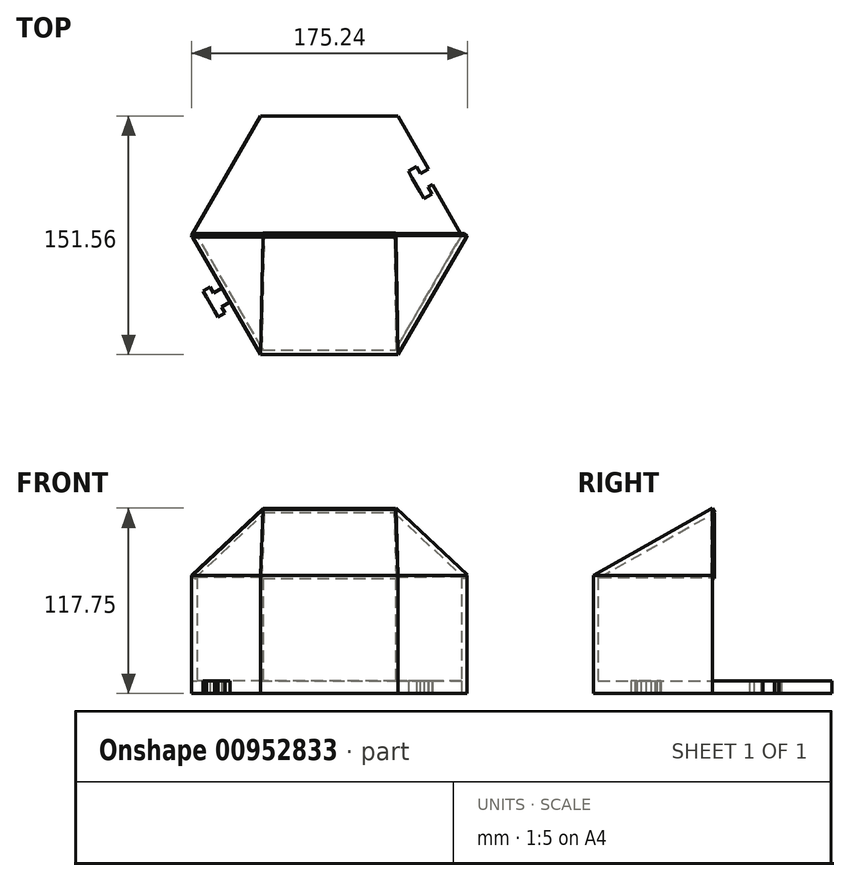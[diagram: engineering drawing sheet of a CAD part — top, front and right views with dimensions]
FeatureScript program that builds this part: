
annotation { "Feature Type Name" : "Feature", "Feature Type Description" : "" }
export const myFeature = defineFeature(function(context is Context, id is Id, definition is map)
    precondition{}
    {
        {
            var Q0;
            Q0=qCreatedBy(makeId("Top.planeOp"),FACE);
            var sketch = newSketch(context, id + "F0", { "sketchPlane" : qUnion([Q0])});
            skCircle(sketch, "E0.cCircle", {"center": v(0, 0) * mm, "radius": 75.78 * mm, "construction": true});
            skLineSegment(sketch, "E0.0", {"start": v(-43.75, 75.78) * mm, "end": v(43.75, 75.78) * mm});
            skLineSegment(sketch, "E0.1", {"start": v(43.75, 75.78) * mm, "end": v(87.5, 0) * mm});
            skLineSegment(sketch, "E0.2", {"start": v(87.5, 0) * mm, "end": v(43.75, -75.78) * mm});
            skLineSegment(sketch, "E0.3", {"start": v(43.75, -75.78) * mm, "end": v(-43.75, -75.78) * mm});
            skLineSegment(sketch, "E0.4", {"start": v(-43.75, -75.78) * mm, "end": v(-87.5, 0) * mm});
            skLineSegment(sketch, "E0.5", {"start": v(-87.5, 0) * mm, "end": v(-43.75, 75.78) * mm});
            skPoint(sketch, "E0.0.midPoint", {"position": v(0, 75.78) * mm});
            skLineSegment(sketch, "E1.0", {"start": v(-84.04, 0) * mm, "end": v(-42.02, 72.78) * mm});
            skLineSegment(sketch, "E1.1", {"start": v(42.02, 72.78) * mm, "end": v(84.04, 0) * mm});
            skLineSegment(sketch, "E1.2", {"start": v(84.04, 0) * mm, "end": v(42.02, -72.78) * mm});
            skLineSegment(sketch, "E1.3", {"start": v(-42.02, 72.78) * mm, "end": v(42.02, 72.78) * mm});
            skLineSegment(sketch, "E1.4", {"start": v(42.02, -72.78) * mm, "end": v(-42.02, -72.78) * mm});
            skLineSegment(sketch, "E1.5", {"start": v(-42.02, -72.78) * mm, "end": v(-84.04, 0) * mm});
            skLineSegment(sketch, "E2", {"start": v(-87.5, 0) * mm, "end": v(-84.04, 0) * mm});
            skLineSegment(sketch, "E3", {"start": v(84.04, 0) * mm, "end": v(87.5, 0) * mm});
            skLineSegment(sketch, "E4", {"start": v(0, 0) * mm, "end": v(0, 72.78) * mm, "construction": true});
            skLineSegment(sketch, "E5", {"start": v(0, 0) * mm, "end": v(42.02, 72.78) * mm, "construction": true});
            skLineSegment(sketch, "E6", {"start": v(0, 0) * mm, "end": v(-42.02, 72.78) * mm, "construction": true});
            skLineSegment(sketch, "E7", {"start": v(0, 36.39) * mm, "end": v(0, 72.78) * mm, "construction": true});
            skLineSegment(sketch, "E8.bottom", {"start": v(25, 48.33) * mm, "end": v(-25, 48.33) * mm});
            skLineSegment(sketch, "E8.top", {"start": v(25, 60.83) * mm, "end": v(-25, 60.83) * mm});
            skLineSegment(sketch, "E8.left", {"start": v(25, 48.33) * mm, "end": v(25, 60.83) * mm});
            skLineSegment(sketch, "E8.right", {"start": v(-25, 48.33) * mm, "end": v(-25, 60.83) * mm});
            skPoint(sketch, "E8.middle", {"position": v(0, 54.58) * mm});
            skLineSegment(sketch, "E9", {"start": v(-65.63, 37.89) * mm, "end": v(-68.13, 33.56) * mm});
            skLineSegment(sketch, "E10.MirrorCS", {"start": v(55.16, 32) * mm, "end": v(57.62, 27.65) * mm});
            skLineSegment(sketch, "E11.MirrorCS", {"start": v(55.16, 32) * mm, "end": v(52.71, 36.37) * mm});
            skLineSegment(sketch, "E12.MirrorCS", {"start": v(57.62, 27.65) * mm, "end": v(68.13, 33.56) * mm});
            skLineSegment(sketch, "E13.MirrorCS", {"start": v(87.5, 0) * mm, "end": v(43.75, 75.78) * mm});
            skLineSegment(sketch, "E14.MirrorCS", {"start": v(52.71, 36.37) * mm, "end": v(63.12, 42.22) * mm});
            skLineSegment(sketch, "E15.MirrorCS", {"start": v(57.97, 39.32) * mm, "end": v(55.52, 43.68) * mm});
            skLineSegment(sketch, "E16.MirrorCS", {"start": v(55.52, 43.68) * mm, "end": v(50.26, 40.72) * mm});
            skLineSegment(sketch, "E17.MirrorCS", {"start": v(52.71, 36.37) * mm, "end": v(50.26, 40.72) * mm});
            skLineSegment(sketch, "E18.MirrorCS", {"start": v(57.62, 27.65) * mm, "end": v(60.07, 23.3) * mm});
            skLineSegment(sketch, "E19.MirrorCS", {"start": v(62.87, 30.6) * mm, "end": v(65.32, 26.25) * mm});
            skLineSegment(sketch, "E20.MirrorCS", {"start": v(65.32, 26.25) * mm, "end": v(60.07, 23.3) * mm});
            skLineSegment(sketch, "E21.MirrorCS", {"start": v(-77.85, -39.32) * mm, "end": v(-68.12, -33.56) * mm});
            skLineSegment(sketch, "E22.MirrorCS", {"start": v(-73.54, -36.77) * mm, "end": v(-75.84, -32.9) * mm});
            skLineSegment(sketch, "E23.MirrorCS", {"start": v(-75.84, -32.9) * mm, "end": v(-80.14, -35.45) * mm});
            skLineSegment(sketch, "E24.MirrorCS", {"start": v(-77.85, -39.32) * mm, "end": v(-80.14, -35.45) * mm});
            skLineSegment(sketch, "E25.MirrorCS", {"start": v(-77.85, -39.32) * mm, "end": v(-72.85, -47.98) * mm});
            skLineSegment(sketch, "E26.MirrorCS", {"start": v(-72.85, -47.98) * mm, "end": v(-70.55, -51.85) * mm});
            skLineSegment(sketch, "E27.MirrorCS", {"start": v(-66.25, -49.3) * mm, "end": v(-70.55, -51.85) * mm});
            skLineSegment(sketch, "E28.MirrorCS", {"start": v(-72.85, -47.98) * mm, "end": v(-63.13, -42.22) * mm});
            skPoint(sketch, "E29.endSnap0", {"position": v(-67.99, -45.1) * mm});
            skLineSegment(sketch, "E30", {"start": v(-72.85, -47.98) * mm, "end": v(-68.54, -45.43) * mm});
            skLineSegment(sketch, "E31", {"start": v(-66.25, -49.3) * mm, "end": v(-68.54, -45.43) * mm});
            skSolve(sketch);
        }
        {
            var Q0;
            Q0=makeQuery(id+"F0.imprint","IMPRINT",FACE,{"disambiguationData":[TD([[makeQuery(id+"F0.imprint","IMPRINT",EDGE,{"derivedFrom":sQuery(id+"F0.wireOp",EDGE,"E1.0")}),-1.0]])]});
            extrude(context, id + "F1", {"entities" : qUnion([Q0]), "depth" : 8 * mm, "offsetDistance" : 25 * mm});
        }
        {
            var Q0;
            Q0=makeQuery(id+"F0.imprint","IMPRINT",FACE,{"disambiguationData":[TD([[makeQuery(id+"F0.imprint","IMPRINT",EDGE,{"derivedFrom":sQuery(id+"F0.wireOp",EDGE,"E0.2")}),-1.0]])]});
            extrude(context, id + "F2", {"entities" : qUnion([Q0]), "operationType" : NewBodyOperationType.ADD, "depth" : 75 * mm, "offsetDistance" : 25 * mm});
        }
        {
            var Q0;
            Q0=qCreatedBy(makeId("Front.planeOp"),FACE);
            var sketch = newSketch(context, id + "F3", { "sketchPlane" : qUnion([Q0])});
            skLineSegment(sketch, "E32", {"start": v(0, 0) * mm, "end": v(0, 144.27) * mm, "construction": true});
            skLineSegment(sketch, "E33", {"start": v(0, 144.27) * mm, "end": v(-94, 144.27) * mm, "construction": true});
            skLineSegment(sketch, "E34", {"start": v(0, 144.27) * mm, "end": v(81.74, 144.27) * mm});
            skLineSegment(sketch, "E35", {"start": v(0, 0) * mm, "end": v(0, 75) * mm, "construction": true});
            skLineSegment(sketch, "E36", {"start": v(0, 75) * mm, "end": v(0, 114.5) * mm, "construction": true});
            skLineSegment(sketch, "E37", {"start": v(0, 75) * mm, "end": v(-87.5, 75) * mm, "construction": true});
            skLineSegment(sketch, "E38", {"start": v(0, 114.5) * mm, "end": v(42.02, 114.5) * mm, "construction": true});
            skLineSegment(sketch, "E39", {"start": v(0, 114.5) * mm, "end": v(-42.02, 114.5) * mm});
            skLineSegment(sketch, "E40", {"start": v(0, 75) * mm, "end": v(-84.04, 75) * mm, "construction": true});
            skLineSegment(sketch, "E41", {"start": v(-42.02, 114.5) * mm, "end": v(-84.04, 75) * mm});
            skLineSegment(sketch, "E42", {"start": v(-42.02, 114.5) * mm, "end": v(-42.02, 117.5) * mm, "construction": true});
            skLineSegment(sketch, "E43", {"start": v(-42.02, 117.5) * mm, "end": v(-87.5, 75) * mm});
            skLineSegment(sketch, "E44", {"start": v(-42.02, 117.5) * mm, "end": v(0, 117.5) * mm});
            skLineSegment(sketch, "E45.MirrorCS", {"start": v(42.02, 117.5) * mm, "end": v(87.5, 75) * mm});
            skLineSegment(sketch, "E46.MirrorCS", {"start": v(42.02, 114.5) * mm, "end": v(84.04, 75) * mm});
            skLineSegment(sketch, "E47.MirrorCS", {"start": v(42.02, 117.5) * mm, "end": v(0, 117.5) * mm});
            skLineSegment(sketch, "E48.MirrorCS", {"start": v(0, 114.5) * mm, "end": v(42.02, 114.5) * mm});
            skLineSegment(sketch, "E49", {"start": v(87.5, 75) * mm, "end": v(84.04, 75) * mm});
            skLineSegment(sketch, "E50", {"start": v(-84.04, 75) * mm, "end": v(-87.5, 75) * mm});
            skSolve(sketch);
        }
        {
            var Q0;
            Q0=makeQuery(id+"F0.imprint","IMPRINT",FACE,{"disambiguationData":[TD([[makeQuery(id+"F0.imprint","IMPRINT",EDGE,{"derivedFrom":sQuery(id+"F0.wireOp",EDGE,"E0.0")}),-1.0]])]});
            extrude(context, id + "F4", {"entities" : qUnion([Q0]), "operationType" : NewBodyOperationType.ADD, "oppositeDirection" : true, "depth" : -8 * mm, "offsetDistance" : 25 * mm});
        }
        {
            var Q0;
            Q0=makeQuery(id+"F2.opExtrude","CAP_EDGE",EDGE,{"disambiguationData":[OSD([sQuery(id+"F0.wireOp",EDGE,"E0.3")])],"isStart":false});
            var Q1;
            Q1=sQuery(id+"F3.wireOp",VERTEX,"E44.end");
            cPlane(context, id + "F5", {"entities" : qUnion([Q0, Q1]), "cplaneType" : CPlaneType.LINE_ANGLE, "offset" : 25 * mm, "angle" : 0 * degree, "width" : 150 * mm, "height" : 150 * mm});
        }
        {
            var Q0;
            Q0=qCreatedBy(id+"F5.planeOp",FACE);
            var sketch = newSketch(context, id + "F6", { "sketchPlane" : qUnion([Q0])});
            skLineSegment(sketch, "E51", {"start": v(0, 29.4) * mm, "end": v(43.75, 29.4) * mm});
            skLineSegment(sketch, "E52", {"start": v(0, 29.4) * mm, "end": v(-43.75, 29.4) * mm});
            skLineSegment(sketch, "E53", {"start": v(-43.75, 29.4) * mm, "end": v(-42.02, -57.48) * mm});
            skLineSegment(sketch, "E54", {"start": v(43.75, 29.4) * mm, "end": v(42.02, -57.48) * mm});
            skLineSegment(sketch, "E55", {"start": v(-42.02, -57.48) * mm, "end": v(42.02, -57.48) * mm});
            skSolve(sketch);
        }
        {
            var Q0;
            Q0=makeQuery(id+"F6.imprint","IMPRINT",FACE,{"disambiguationData":[TD([[makeQuery(id+"F6.imprint","IMPRINT",EDGE,{"derivedFrom":sQuery(id+"F6.wireOp",EDGE,"E51")}),-1.0]])]});
            extrude(context, id + "F7", {"entities" : qUnion([Q0]), "operationType" : NewBodyOperationType.ADD, "depth" : 3 * mm, "offsetDistance" : 25 * mm});
        }
        {
            var Q0;
            Q0=makeQuery(id+"F3.imprint","IMPRINT",FACE,{"disambiguationData":[TD([[makeQuery(id+"F3.imprint","IMPRINT",EDGE,{"derivedFrom":sQuery(id+"F3.wireOp",EDGE,"E39")}),-1.0]])]});
            extrude(context, id + "F8", {"entities" : qUnion([Q0]), "operationType" : NewBodyOperationType.ADD, "depth" : 1 * mm, "offsetDistance" : 25 * mm});
        }
        {
            var Q0;
            Q0=makeQuery(id+"F8.opExtrude","CAP_EDGE",EDGE,{"disambiguationData":[OSD([sQuery(id+"F3.wireOp",EDGE,"E43")])],"isStart":true});
            var Q1;
            Q1=makeQuery(id+"F7.boolean.opBoolean","MERGE",VERTEX,{"derivedFrom":[makeQuery(id+"F2.opExtrude","CAP_VERTEX",VERTEX,{"disambiguationData":[OSD([sQuery(id+"F0.wireOp",EDGE,"E0.3"),sQuery(id+"F0.wireOp",EDGE,"E0.4")])],"isStart":false}),makeQuery(id+"F7.opExtrude","CAP_VERTEX",VERTEX,{"disambiguationData":[OSD([sQuery(id+"F6.wireOp",EDGE,"E52"),sQuery(id+"F6.wireOp",EDGE,"E53")])],"isStart":true})]});
            cPlane(context, id + "F9", {"entities" : qUnion([Q0, Q1]), "cplaneType" : CPlaneType.LINE_ANGLE, "offset" : 25 * mm, "angle" : 0 * degree, "width" : 150 * mm, "height" : 150 * mm});
        }
        {
            var Q0;
            Q0=qCreatedBy(id+"F9.planeOp",FACE);
            var sketch = newSketch(context, id + "F10", { "sketchPlane" : qUnion([Q0])});
            skLineSegment(sketch, "E56", {"start": v(-25.66, 35.61) * mm, "end": v(30.99, -31.08) * mm});
            skLineSegment(sketch, "E57", {"start": v(-25.66, 35.61) * mm, "end": v(33.23, 55.79) * mm});
            skLineSegment(sketch, "E58", {"start": v(33.23, 55.79) * mm, "end": v(30.99, -31.08) * mm});
            skSolve(sketch);
        }
        {
            var Q0;
            Q0=qSketchRegion(id+"F10",true);
            extrude(context, id + "F11", {"entities" : qUnion([Q0]), "operationType" : NewBodyOperationType.ADD, "depth" : -3 * mm, "offsetDistance" : 25 * mm});
        }
        {
            var Q0;
            Q0=makeQuery(id+"F8.opExtrude","CAP_EDGE",EDGE,{"disambiguationData":[OSD([sQuery(id+"F3.wireOp",EDGE,"E45.MirrorCS")])],"isStart":false});
            var Q1;
            Q1=makeQuery(id+"F7.boolean.opBoolean","MERGE",VERTEX,{"derivedFrom":[makeQuery(id+"F2.opExtrude","CAP_VERTEX",VERTEX,{"disambiguationData":[OSD([sQuery(id+"F0.wireOp",EDGE,"E0.2"),sQuery(id+"F0.wireOp",EDGE,"E0.3")])],"isStart":false}),makeQuery(id+"F7.opExtrude","CAP_VERTEX",VERTEX,{"disambiguationData":[OSD([sQuery(id+"F6.wireOp",EDGE,"E51"),sQuery(id+"F6.wireOp",EDGE,"E54")])],"isStart":true})]});
            cPlane(context, id + "F12", {"entities" : qUnion([Q0, Q1]), "cplaneType" : CPlaneType.LINE_ANGLE, "offset" : 25 * mm, "angle" : 0 * degree, "width" : 150 * mm, "height" : 150 * mm});
        }
        {
            var Q0;
            Q0=qCreatedBy(id+"F12.planeOp",FACE);
            var sketch = newSketch(context, id + "F13", { "sketchPlane" : qUnion([Q0])});
            skLineSegment(sketch, "E59", {"start": v(-32.88, -56.36) * mm, "end": v(25.94, -35.98) * mm});
            skLineSegment(sketch, "E60", {"start": v(25.94, -35.98) * mm, "end": v(-30.94, 30.51) * mm});
            skLineSegment(sketch, "E61", {"start": v(-30.94, 30.51) * mm, "end": v(-32.88, -56.36) * mm});
            skSolve(sketch);
        }
        {
            var Q0;
            Q0=qSketchRegion(id+"F13",true);
            extrude(context, id + "F14", {"entities" : qUnion([Q0]), "operationType" : NewBodyOperationType.ADD, "depth" : 3 * mm, "offsetDistance" : 25 * mm});
        }
        {
            var Q0;
            Q0=makeQuery(id+"F0.imprint","IMPRINT",FACE,{"disambiguationData":[TD([[makeQuery(id+"F0.imprint","IMPRINT",EDGE,{"derivedFrom":sQuery(id+"F0.wireOp",EDGE,"E8.bottom")}),-1.0]])]});
            extrude(context, id + "F15", {"entities" : qUnion([Q0]), "operationType" : NewBodyOperationType.ADD, "depth" : 8 * mm, "offsetDistance" : 25 * mm});
        }
        {
            var Q0;
            {var subQ5=sQuery(id+"F0.wireOp",EDGE,"E23.MirrorCS");Q0=makeQuery(id+"F0.imprint","IMPRINT",FACE,{"disambiguationData":[TD([[makeQuery(id+"F0.imprint","IMPRINT",EDGE,{"derivedFrom":subQ5}),1.0]])]});}
            var Q1;
            {var subQ4=sQuery(id+"F0.wireOp",EDGE,"E25.MirrorCS");Q1=makeQuery(id+"F0.imprint","IMPRINT",FACE,{"disambiguationData":[TD([[makeQuery(id+"F0.imprint","IMPRINT",EDGE,{"derivedFrom":subQ4}),1.0]])]});}
            var Q2;
            {var subQ0=sQuery(id+"F0.wireOp",EDGE,"E26.MirrorCS");Q2=makeQuery(id+"F0.imprint","IMPRINT",FACE,{"disambiguationData":[TD([[makeQuery(id+"F0.imprint","IMPRINT",EDGE,{"derivedFrom":subQ0}),1.0]])]});}
            var Q3;
            {var subQ5=sQuery(id+"F0.wireOp",EDGE,"bff1d7ab-137b-4689-a84f-e4ae87ef17b27.MirrorCS");Q3=makeQuery(id+"F0.imprint","IMPRINT",FACE,{"disambiguationData":[TD([[makeQuery(id+"F0.imprint","IMPRINT",EDGE,{"derivedFrom":subQ5}),-1.0]])]});}
            var Q4;
            {var subQ0=sQuery(id+"F0.wireOp",EDGE,"bff1d7ab-137b-4689-a84f-e4ae87ef17b24.MirrorCS");Q4=makeQuery(id+"F0.imprint","IMPRINT",FACE,{"disambiguationData":[TD([[makeQuery(id+"F0.imprint","IMPRINT",EDGE,{"derivedFrom":subQ0}),-1.0]])]});}
            var Q5;
            {var subQ0=sQuery(id+"F0.wireOp",EDGE,"bff1d7ab-137b-4689-a84f-e4ae87ef17b20.MirrorCS");Q5=makeQuery(id+"F0.imprint","IMPRINT",FACE,{"disambiguationData":[TD([[makeQuery(id+"F0.imprint","IMPRINT",EDGE,{"derivedFrom":subQ0}),1.0]])]});}
            extrude(context, id + "F16", {"entities" : qUnion([Q0, Q1, Q2, Q3, Q4, Q5]), "operationType" : NewBodyOperationType.ADD, "depth" : 8 * mm, "offsetDistance" : 25 * mm});
        }
    });
